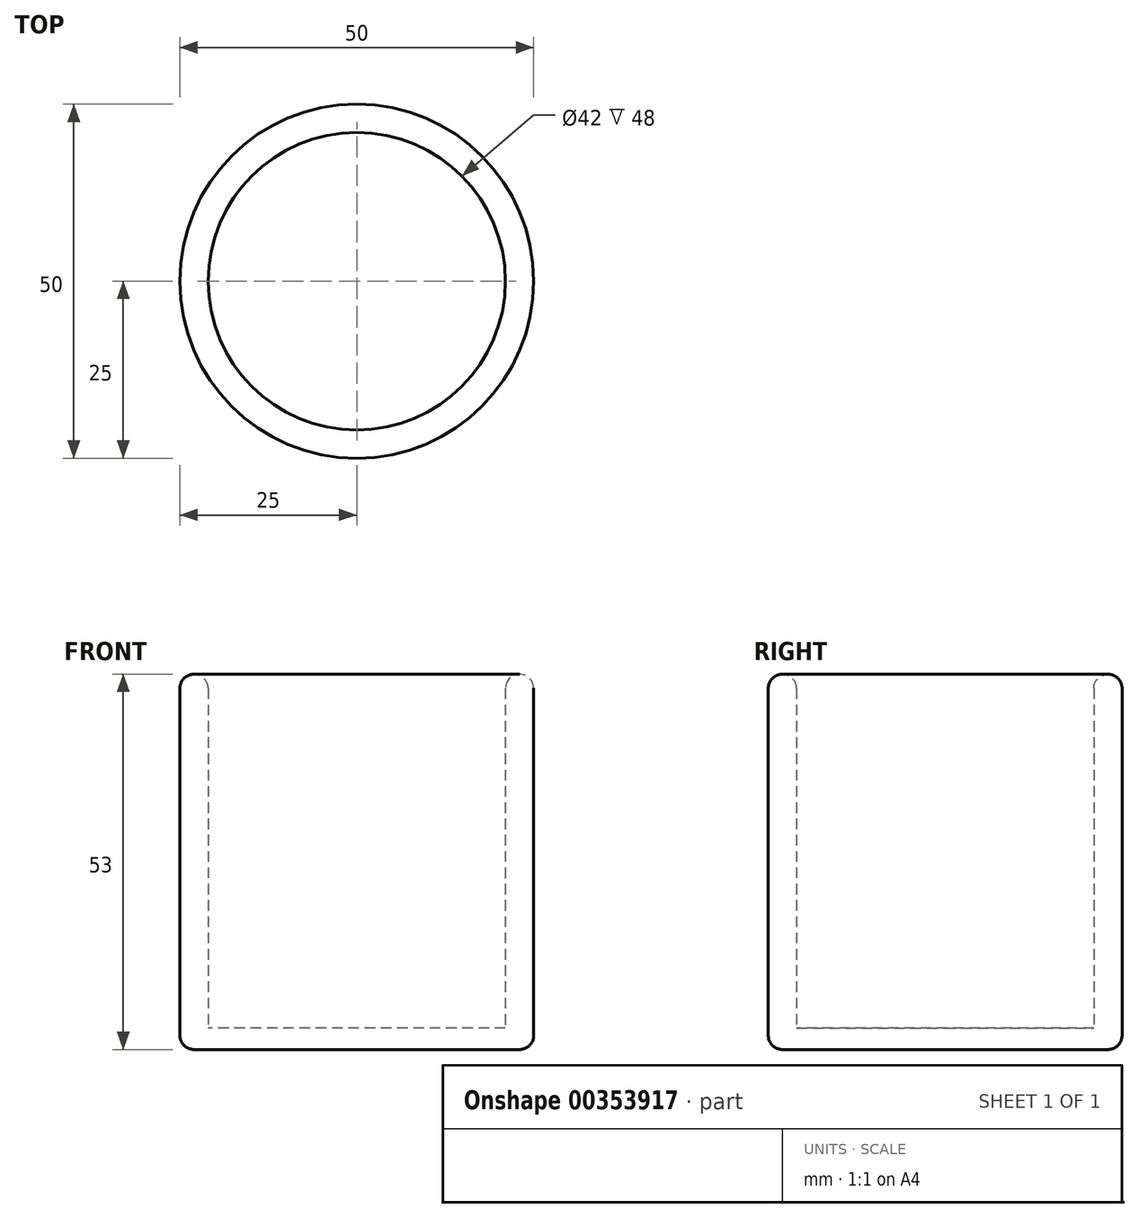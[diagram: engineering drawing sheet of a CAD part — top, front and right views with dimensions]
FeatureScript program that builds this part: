
annotation { "Feature Type Name" : "Feature", "Feature Type Description" : "" }
export const myFeature = defineFeature(function(context is Context, id is Id, definition is map)
    precondition{}
    {
        {
            var Q0;
            Q0=qCreatedBy(makeId("Top.planeOp"),FACE);
            var sketch = newSketch(context, id + "F0", { "sketchPlane" : qUnion([Q0])});
            skCircle(sketch, "E0", {"center": v(0, 0) * mm, "radius": 25 * mm});
            skSolve(sketch);
        }
        {
            var Q0;
            Q0 = qSketchRegion(id + "F0", true);
            var Q1;
            Q1=makeQuery(id+"F0.imprint","IMPRINT",FACE,{"disambiguationData":[TD([[makeQuery(id+"F0.imprint","IMPRINT",EDGE,{"derivedFrom":sQuery(id+"F0.wireOp",EDGE,"E0")}),1.0]])]});
            extrude(context, id + "F1", {"entities" : qUnion([Q0, Q1]), "depth" : 3 * mm});
        }
        {
            var Q0;
            Q0=makeQuery(id+"F1.opExtrude","CAP_FACE",FACE,{"disambiguationData":[OSD([sQuery(id+"F0.wireOp",EDGE,"E0")])],"isStart":false});
            var sketch = newSketch(context, id + "F2", { "sketchPlane" : qUnion([Q0])});
            skCircle(sketch, "E1", {"center": v(0, 0) * mm, "radius": 21 * mm});
            skSolve(sketch);
        }
        {
            var Q0;
            Q0=makeQuery(id+"F2.imprint","IMPRINT",FACE,{"disambiguationData":[TD([[makeQuery(id+"F2.imprint","IMPRINT",EDGE,{"derivedFrom":sQuery(id+"F2.wireOp",EDGE,"E1")}),-1.0]])]});
            extrude(context, id + "F3", {"entities" : qUnion([Q0]), "operationType" : NewBodyOperationType.ADD, "depth" : 50 * mm});
        }
        {
            var Q0;
            Q0=makeQuery(id+"F3.opExtrude","CAP_EDGE",EDGE,{"disambiguationData":[OSD([sQuery(id+"F0.wireOp",EDGE,"E0")])],"isStart":false});
            var Q1;
            Q1=makeQuery(id+"F3.opExtrude","CAP_EDGE",EDGE,{"disambiguationData":[OSD([sQuery(id+"F2.wireOp",EDGE,"E1")])],"isStart":false});
            var Q2;
            Q2=makeQuery(id+"F3.opExtrude","CAP_EDGE",EDGE,{"disambiguationData":[OSD([sQuery(id+"F2.wireOp",EDGE,"E1")])],"isStart":true});
            var Q3;
            Q3=makeQuery(id+"F1.opExtrude","CAP_EDGE",EDGE,{"disambiguationData":[OSD([sQuery(id+"F0.wireOp",EDGE,"E0")])],"isStart":true});
            fillet(context, id + "F4", {"entities" : qUnion([Q0, Q1, Q2, Q3]), "radius" : 2 * mm, "tangentPropagation" : true, "allowEdgeOverflow" : false});
        }
    });
